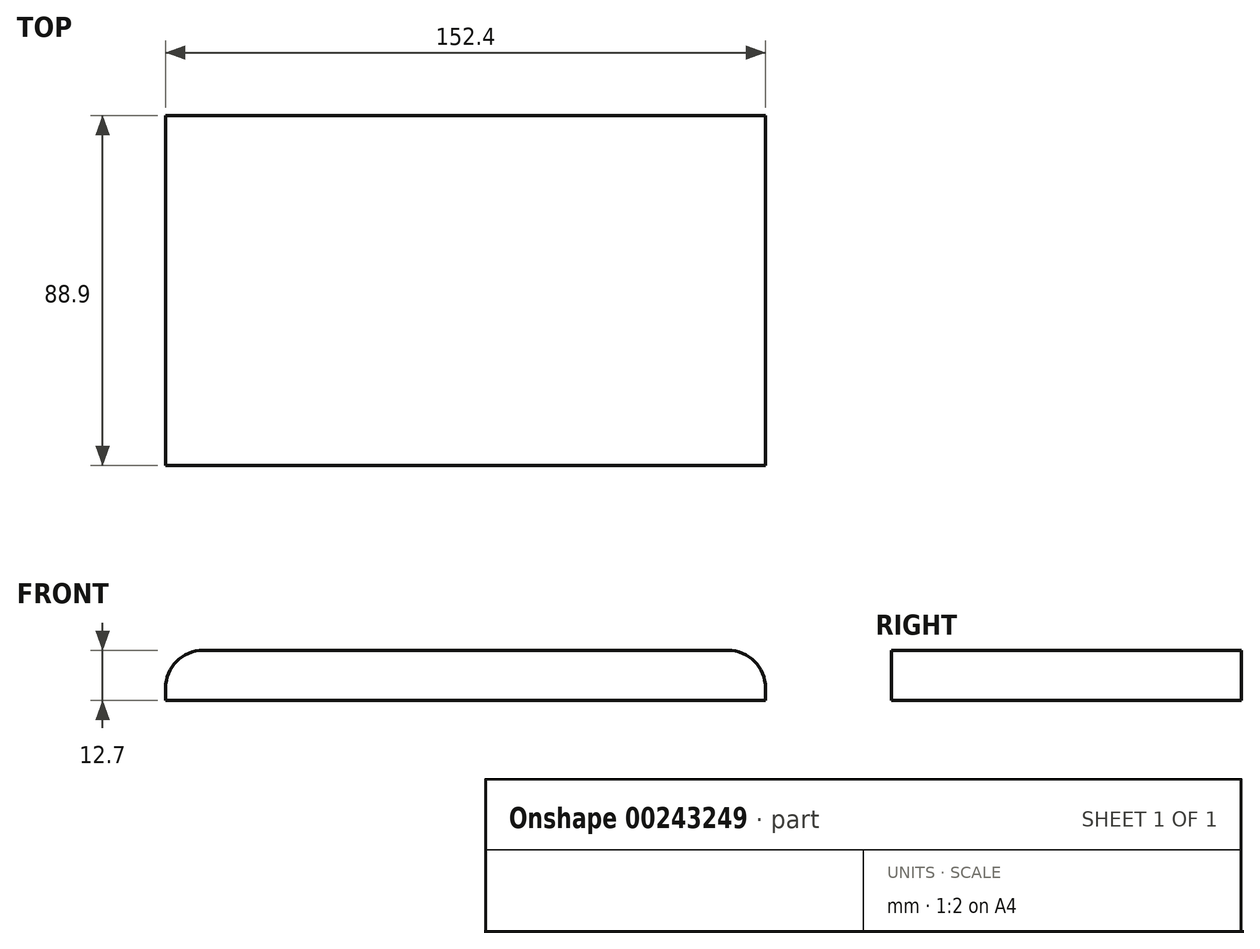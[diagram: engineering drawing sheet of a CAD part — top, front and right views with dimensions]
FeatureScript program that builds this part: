
annotation { "Feature Type Name" : "Feature", "Feature Type Description" : "" }
export const myFeature = defineFeature(function(context is Context, id is Id, definition is map)
    precondition{}
    {
        {
            var Q0;
            Q0=qCreatedBy(makeId("Front.planeOp"),FACE);
            var sketch = newSketch(context, id + "F0", { "sketchPlane" : qUnion([Q0])});
            skLineSegment(sketch, "E0", {"start": v(0, 0) * mm, "end": v(0, -12.7) * mm});
            skLineSegment(sketch, "E1", {"start": v(0, -12.7) * mm, "end": v(152.4, -12.7) * mm});
            skLineSegment(sketch, "E2", {"start": v(152.4, -12.7) * mm, "end": v(152.4, 0) * mm});
            skLineSegment(sketch, "E3", {"start": v(152.4, 0) * mm, "end": v(0, 0) * mm});
            skSolve(sketch);
        }
        {
            var Q0;
            Q0 = qSketchRegion(id + "F0", true);
            extrude(context, id + "F1", {"entities" : qUnion([Q0]), "depth" : 88.9 * mm});
        }
        {
            var Q0;
            Q0=makeQuery(id+"F1.opExtrude","SWEPT_EDGE",EDGE,{"disambiguationData":[OSD([sQuery(id+"F0.wireOp",EDGE,"E2"),sQuery(id+"F0.wireOp",EDGE,"E3")])]});
            var Q1;
            Q1=makeQuery(id+"F1.opExtrude","SWEPT_EDGE",EDGE,{"disambiguationData":[OSD([sQuery(id+"F0.wireOp",EDGE,"E0"),sQuery(id+"F0.wireOp",EDGE,"E3")])]});
            fillet(context, id + "F2", {"entities" : qUnion([Q0, Q1]), "radius" : 9.52 * mm, "tangentPropagation" : true, "allowEdgeOverflow" : false});
        }
    });
